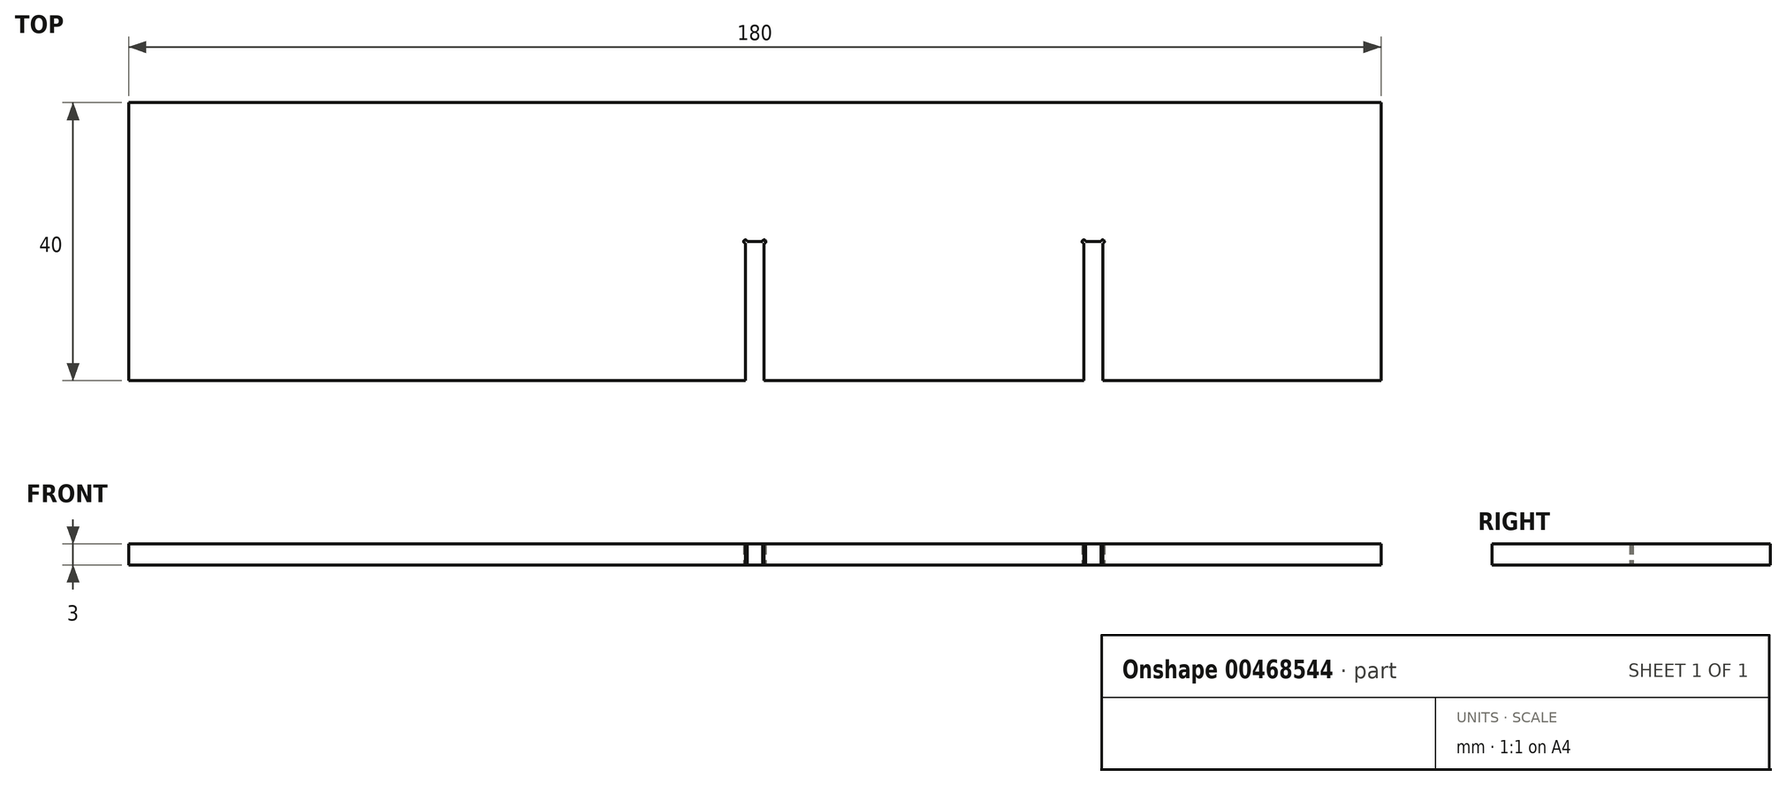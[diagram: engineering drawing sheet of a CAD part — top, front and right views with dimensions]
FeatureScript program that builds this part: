
annotation { "Feature Type Name" : "Feature", "Feature Type Description" : "" }
export const myFeature = defineFeature(function(context is Context, id is Id, definition is map)
    precondition{}
    {
        {
            var Q0;
            Q0=qCreatedBy(makeId("Top.planeOp"),FACE);
            var sketch = newSketch(context, id + "F0", { "sketchPlane" : qUnion([Q0])});
            skLineSegment(sketch, "E0.bottom", {"start": v(-90, 0) * mm, "end": v(90, 0) * mm});
            skLineSegment(sketch, "E0.top", {"start": v(-90, -40) * mm, "end": v(-1.35, -40) * mm});
            skLineSegment(sketch, "E0.left", {"start": v(-90, 0) * mm, "end": v(-90, -40) * mm});
            skLineSegment(sketch, "E0.right", {"start": v(90, 0) * mm, "end": v(90, -40) * mm});
            skLineSegment(sketch, "E1.top", {"start": v(-1.35, -20) * mm, "end": v(1.35, -20) * mm});
            skLineSegment(sketch, "E1.left", {"start": v(-1.35, -40) * mm, "end": v(-1.35, -20) * mm});
            skLineSegment(sketch, "E1.right", {"start": v(1.35, -40) * mm, "end": v(1.35, -20) * mm});
            skPoint(sketch, "E2", {"position": v(0, -20) * mm});
            skLineSegment(sketch, "E3.trimOffspring", {"start": v(1.35, -40) * mm, "end": v(47.3, -40) * mm});
            skCircle(sketch, "E4", {"center": v(1.35, -20) * mm, "radius": 0.25 * mm});
            skCircle(sketch, "E5", {"center": v(-1.35, -20) * mm, "radius": 0.25 * mm});
            skPoint(sketch, "E6", {"position": v(50, -40) * mm});
            skLineSegment(sketch, "E7.top", {"start": v(50, -20) * mm, "end": v(47.3, -20) * mm});
            skLineSegment(sketch, "E7.left", {"start": v(50, -40) * mm, "end": v(50, -20) * mm});
            skLineSegment(sketch, "E7.right", {"start": v(47.3, -40) * mm, "end": v(47.3, -20) * mm});
            skCircle(sketch, "E8", {"center": v(50, -20) * mm, "radius": 0.25 * mm});
            skCircle(sketch, "E9", {"center": v(47.3, -20) * mm, "radius": 0.25 * mm});
            skLineSegment(sketch, "E10.trimOffspring", {"start": v(50, -40) * mm, "end": v(90, -40) * mm});
            skSolve(sketch);
        }
        {
            var Q0;
            Q0=makeQuery(id+"F0.imprint","IMPRINT",FACE,{"disambiguationData":[TD([[makeQuery(id+"F0.imprint","IMPRINT",EDGE,{"derivedFrom":sQuery(id+"F0.wireOp",EDGE,"E0.bottom")}),-1.0]])]});
            extrude(context, id + "F1", {"entities" : qUnion([Q0]), "depth" : 3 * mm, "offsetDistance" : 25 * mm});
        }
    });
